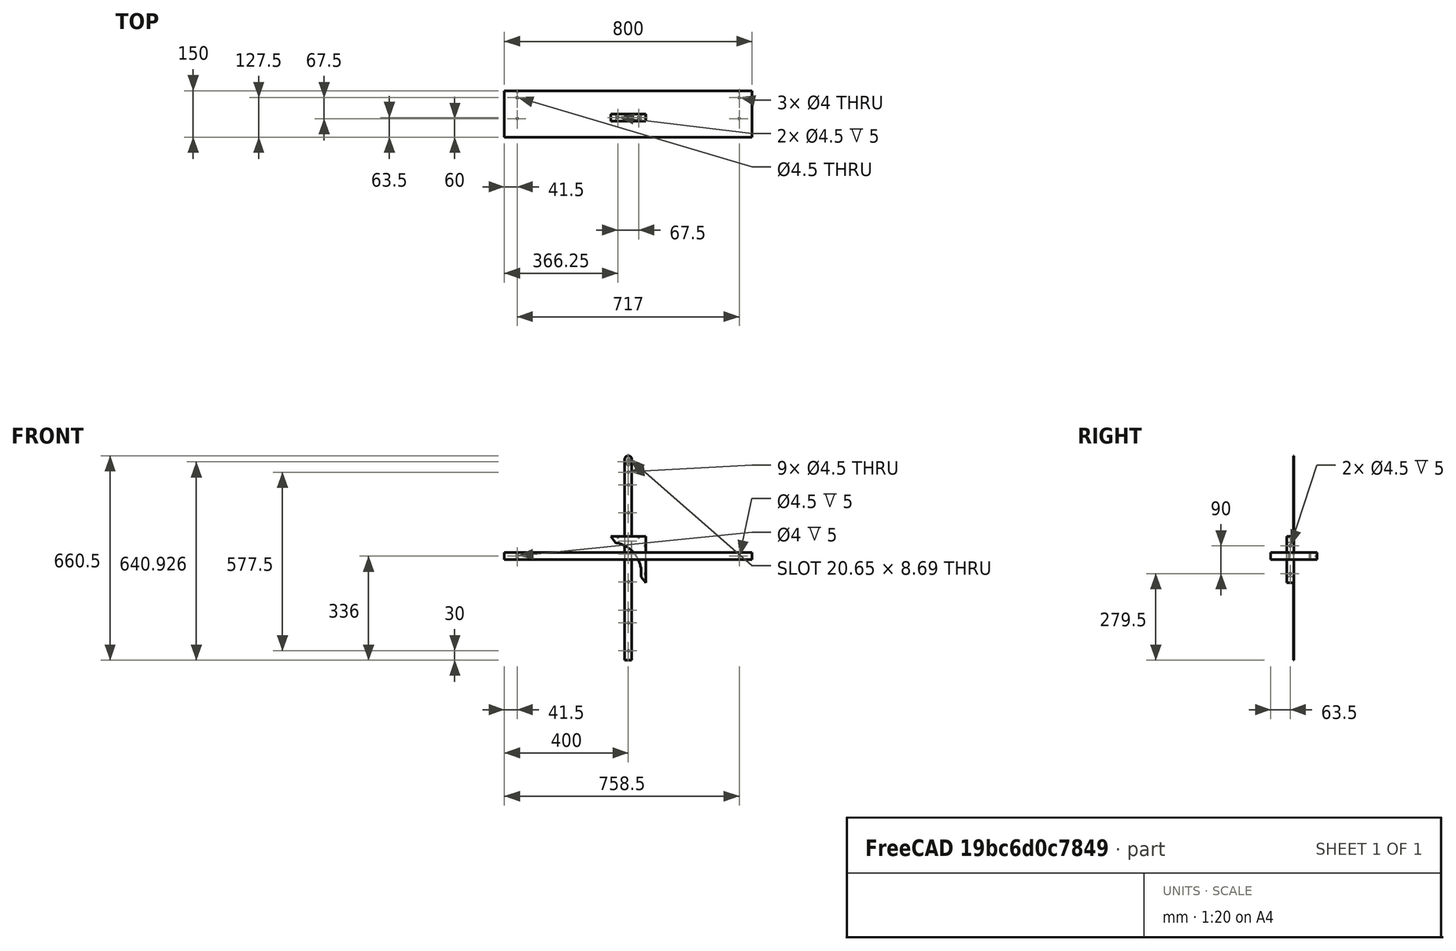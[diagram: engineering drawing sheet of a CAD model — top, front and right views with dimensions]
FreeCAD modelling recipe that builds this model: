
FCSTD DOCUMENT  (FreeCAD 1.0R39109 (Git))
Label: shelf
License: All rights reserved
LicenseURL: https://en.wikipedia.org/wiki/All_rights_reserved
objects: App::FeaturePython×30, TechDraw::DrawViewDimension×30, App::Link×11, Sketcher::SketchObject×7, PartDesign::Pocket×4, TechDraw::DrawProjGroupItem×4, PartDesign::Pad×3, PartDesign::Body×3, TechDraw::DrawSVGTemplate×3, TechDraw::DrawPage×3, Spreadsheet::Sheet×1, TechDraw::DrawProjGroup×1, Assembly::JointGroup×1, Assembly::AssemblyObject×1
note: 84 computed .brp shape members not serialized (recipe doc carries the construction recipe); baked Part::Feature solids carry a one-line shape summary decoded from their .brp

FEATURE [Sketcher::SketchObject] Sketch  label="Top view"
  ArcFitTolerance = 1e-06
  AttachmentSupport = -> [XY_Plane]
  FullyConstrained = true
  MakeInternals = false
  MapMode = 5
  expr: Constraints[12] = <<data>>.pw
  expr: Constraints[13] = <<data>>.pl
  sketch-geometry (6):
    g0: LineSegment StartX=400 StartY=-75 StartZ=0 EndX=400 EndY=75 EndZ=0
    g1: LineSegment StartX=400 StartY=75 StartZ=0 EndX=-400 EndY=75 EndZ=0
    g2: LineSegment StartX=-400 StartY=75 StartZ=0 EndX=-400 EndY=-75 EndZ=0
    g3: LineSegment StartX=-400 StartY=-75 StartZ=0 EndX=400 EndY=-75 EndZ=0
    g4: GeomPoint [constr] X=-2.3e-15 Y=75 Z=0
    g5: GeomPoint [constr] X=400 Y=0 Z=0
  constraints (14):
    c: Coincident(g0,g1)
    c: Coincident(g1,g2)
    c: Coincident(g2,g3)
    c: Coincident(g3,g0)
    c: Vertical(g0)
    c: Vertical(g2)
    c: Horizontal(g1)
    c: Horizontal(g3)
    c: Symmetric(g1,g1,g4)
    c: Symmetric(g0,g0,g5)
    c: Vertical(g4,g-1)
    c: Horizontal(g5,g-1)
    c: DistanceY(g2,g2) = 150
    c: DistanceX(g3,g3) = 800
FEATURE [Spreadsheet::Sheet] Spreadsheet  label="data"
  cells = A1='plank thickness; B1(pt)==23 mm; D1='strip top length; E1(stl)==3 cm; A2='plank length; B2(pl)==80 cm; D2='screw diameter; E2(sd)==4.5 mm; A3='plank width; B3(pw)==15 cm; A4='plank spacing; B4(ps)==20 cm; A5='strip thickness; B5(strip_thickness)==2 mm; A7='triangle ratio; B7(tr)==3 / 4; A8='hole ratio; B8(hr)==1 / 5; A9='triangle hole distance; B9(thd)==(1 - hr * 2) * ps * tr; D9='triangle plank hole distance; E9(tphd)==(1 - hr * 2) * pw * tr; A10='triangle holes pair interval; B10(thpi)==2 * ps * tr * hr + ps * (1 - tr) + pt; A12='tirangle shift; B12(ts)==30 mm
FEATURE [PartDesign::Pad] Pad
  Direction = (0,0,1)
  Length = 23
  Length2 = 10
  Profile = -> Sketch
  ReferenceAxis = -> Sketch [N_Axis]
  Refine = true
  Suppressed = false
  Type = 0
  expr: Length = <<data>>.pt
FEATURE [Sketcher::SketchObject] Sketch001  label="Top view001"
  ArcFitTolerance = 1e-06
  AttachmentSupport = -> [XZ_Plane001]
  FullyConstrained = true
  MakeInternals = false
  MapMode = 5
  Placement = pos=(0,0,0) rot=(1,0,0;1.5708rad)
  expr: Constraints[14] = <<data>>.pw * <<data>>.tr
  expr: Constraints[15] = <<data>>.ps * <<data>>.tr
  sketch-geometry (10):
    g0: LineSegment [constr] StartX=-56.25 StartY=75 StartZ=0 EndX=-56.25 EndY=-75 EndZ=0
    g1: LineSegment [constr] StartX=-56.25 StartY=-75 StartZ=0 EndX=56.25 EndY=-75 EndZ=0
    g2: LineSegment StartX=56.25 StartY=-75 StartZ=0 EndX=56.25 EndY=75 EndZ=0
    g3: LineSegment StartX=56.25 StartY=75 StartZ=0 EndX=-56.25 EndY=75 EndZ=0
    g4: LineSegment [constr] StartX=-56.25 StartY=75 StartZ=0 EndX=56.25 EndY=-75 EndZ=0
    g5: GeomPoint [constr] X=0 Y=75 Z=0
    g6: GeomPoint [constr] X=56.25 Y=0 Z=0
    g7: ArcOfCircle CenterX=-56.25 CenterY=-42.1875 CenterZ=0 NormalX=0 NormalY=0 NormalZ=1 AngleXU=0 Radius=98.3382 StartAngle=6.15252 EndAngle=7.70085
    g8: LineSegment StartX=-56.25 StartY=75 StartZ=0 EndX=-41.25 EndY=55 EndZ=0
    g9: LineSegment StartX=41.25 StartY=-55 StartZ=0 EndX=56.25 EndY=-75 EndZ=0
  constraints (25):
    c: Coincident(g0,g1)
    c: Coincident(g1,g2)
    c: Coincident(g2,g3)
    c: Coincident(g3,g0)
    c: Vertical(g0)
    c: Vertical(g2)
    c: Horizontal(g1)
    c: Horizontal(g3)
    c: Coincident(g4,g0)
    c: Coincident(g4,g1)
    c: Symmetric(g3,g3,g5)
    c: Symmetric(g2,g2,g6)
    c: Vertical(g5,g-1)
    c: Horizontal(g6,g-1)
    c: DistanceX(g3,g3) = 112.5
    c: DistanceY(g2,g2) = 150
    c: PointOnObject(g7,g4)
    c: PointOnObject(g7,g4)
    c: Coincident(g8,g0)
    c: Coincident(g8,g7)
    c: Coincident(g9,g7)
    c: Coincident(g9,g1)
    c: Distance(g9,g9) = 25
    c: Equal(g8,g9)
    c: PointOnObject(g7,g0)
FEATURE [PartDesign::Pad] Pad001
  Direction = (0,-1,2e-16)
  Length = 23
  Length2 = 10
  Placement = pos=(0,0,0) rot=(1,0,0;1.5708rad)
  Profile = -> Sketch001
  ReferenceAxis = -> Sketch001 [N_Axis]
  Refine = true
  Suppressed = false
  Type = 0
  expr: Length = <<data>>.pt
FEATURE [Sketcher::SketchObject] Sketch002
  ArcFitTolerance = 1e-06
  AttachmentSupport = -> [XZ_Plane002]
  FullyConstrained = true
  MakeInternals = false
  MapMode = 5
  Placement = pos=(0,0,0) rot=(1,0,0;1.5708rad)
  expr: Constraints[10] = <<data>>.pt
  expr: Constraints[11] = <<data>>.stl + <<data>>.pt * 3 + <<data>>.ps * 2 + <<data>>.tr * <<data>>.ps
  expr: Constraints[17] = <<data>>.sd
  expr: Constraints[18] = <<data>>.stl + <<data>>.pt + <<data>>.ps * <<data>>.tr / 5
  expr: Constraints[20] = <<data>>.sd
  expr: Constraints[21] = <<data>>.thd
  expr: Constraints[23] = <<data>>.thpi
  expr: Constraints[24] = <<data>>.sd
  expr: Constraints[26] = <<data>>.sd
  expr: Constraints[27] = <<data>>.thd
  expr: Constraints[29] = <<data>>.sd
  expr: Constraints[31] = <<data>>.sd
  expr: Constraints[32] = <<data>>.thd
  expr: Constraints[33] = <<data>>.thpi
  expr: Constraints[36] = <<data>>.pt / 2 + <<data>>.ps * <<data>>.tr * <<data>>.hr
  expr: Constraints[38] = <<data>>.sd
  expr: Constraints[39] = <<data>>.pt / 2 + <<data>>.ps * <<data>>.tr * <<data>>.hr
  expr: Constraints[41] = <<data>>.sd
  expr: Constraints[42] = <<data>>.pt / 2 + <<data>>.ps * <<data>>.tr * <<data>>.hr
  expr: Constraints[46] = <<data>>.sd
  expr: Constraints[52] = <<data>>.sd
  expr: Constraints[53] = 10 mm
  sketch-geometry (20):
    g0: LineSegment StartX=-11.5 StartY=324.5 StartZ=0 EndX=-11.5 EndY=-324.5 EndZ=0
    g1: LineSegment StartX=-11.5 StartY=-324.5 StartZ=0 EndX=11.5 EndY=-324.5 EndZ=0
    g2: LineSegment StartX=11.5 StartY=-324.5 StartZ=0 EndX=11.5 EndY=324.5 EndZ=0
    g3: LineSegment [constr] StartX=11.5 StartY=324.5 StartZ=0 EndX=-11.5 EndY=324.5 EndZ=0
    g4: ArcOfCircle CenterX=-4e-16 CenterY=324.5 CenterZ=0 NormalX=0 NormalY=0 NormalZ=1 AngleXU=0 Radius=11.5 StartAngle=0 EndAngle=3.14159
    g5: GeomPoint X=-11.5 Y=0 Z=0
    g6: GeomPoint X=0 Y=-324.5 Z=0
    g7: Circle CenterX=0 CenterY=241.5 CenterZ=0 NormalX=0 NormalY=0 NormalZ=1 AngleXU=0 Radius=2.25
    g8: Circle CenterX=0 CenterY=151.5 CenterZ=0 NormalX=0 NormalY=0 NormalZ=1 AngleXU=0 Radius=2.25
    g9: Circle CenterX=0 CenterY=18.5 CenterZ=0 NormalX=0 NormalY=0 NormalZ=1 AngleXU=0 Radius=2.25
    g10: Circle CenterX=0 CenterY=-71.5 CenterZ=0 NormalX=0 NormalY=0 NormalZ=1 AngleXU=0 Radius=2.25
    g11: Circle CenterX=0 CenterY=-204.5 CenterZ=0 NormalX=0 NormalY=0 NormalZ=1 AngleXU=0 Radius=2.25
    g12: Circle CenterX=0 CenterY=-294.5 CenterZ=0 NormalX=0 NormalY=0 NormalZ=1 AngleXU=0 Radius=2.25
    g13: Circle CenterX=0 CenterY=283 CenterZ=0 NormalX=0 NormalY=0 NormalZ=1 AngleXU=0 Radius=2.25
    g14: Circle CenterX=0 CenterY=60 CenterZ=0 NormalX=0 NormalY=0 NormalZ=1 AngleXU=0 Radius=2.25
    g15: Circle CenterX=0 CenterY=-163 CenterZ=0 NormalX=0 NormalY=0 NormalZ=1 AngleXU=0 Radius=2.25
    g16: ArcOfCircle CenterX=-4e-16 CenterY=324.5 CenterZ=0 NormalX=0 NormalY=0 NormalZ=1 AngleXU=0 Radius=2.25 StartAngle=-1.15e-14 EndAngle=3.14159
    g17: LineSegment StartX=2.25 StartY=324.5 StartZ=0 EndX=2.25 EndY=314.5 EndZ=0
    g18: LineSegment StartX=-2.25 StartY=324.5 StartZ=0 EndX=-2.25 EndY=314.5 EndZ=0
    g19: ArcOfCircle CenterX=0 CenterY=310.603 CenterZ=0 NormalX=0 NormalY=0 NormalZ=1 AngleXU=0 Radius=4.5 StartAngle=2.0944 EndAngle=7.33038
  constraints (54):
    c: Coincident(g0,g1)
    c: Coincident(g1,g2)
    c: Coincident(g2,g3)
    c: Coincident(g3,g0)
    c: Vertical(g0)
    c: Vertical(g2)
    c: Horizontal(g1)
    c: Horizontal(g3)
    c: Coincident(g4,g2)
    c: Tangent(g4,g0) = -1.5708
    c: DistanceX(g1,g1) = 23
    c: DistanceY(g2,g2) = 649
    c: Symmetric(g0,g0,g5)
    c: Symmetric(g1,g1,g6)
    c: Horizontal(g5,g-1)
    c: Vertical(g6,g-1)
    c: PointOnObject(g7,g-2)
    c: Diameter(g7) = 4.5
    c: DistanceY(g7,g4) = 83
    c: PointOnObject(g8,g-2)
    c: Diameter(g8) = 4.5
    c: DistanceY(g8,g7) = 90
    c: PointOnObject(g9,g-2)
    c: DistanceY(g9,g8) = 133
    c: Diameter(g9) = 4.5
    c: PointOnObject(g10,g-2)
    c: Diameter(g10) = 4.5
    c: DistanceY(g10,g9) = 90
    c: PointOnObject(g11,g-2)
    c: Diameter(g11) = 4.5
    c: PointOnObject(g12,g-2)
    c: Diameter(g12) = 4.5
    c: DistanceY(g12,g11) = 90
    c: DistanceY(g11,g10) = 133
    c: PointOnObject(g13,g-2)
    c: Equal(g13,g7)
    c: DistanceY(g7,g13) = 41.5
    c: PointOnObject(g14,g-2)
    c: Diameter(g14) = 4.5
    c: DistanceY(g9,g14) = 41.5
    c: PointOnObject(g15,g-2)
    c: Diameter(g15) = 4.5
    c: DistanceY(g11,g15) = 41.5
    c: Tangent(g16,g17) = 1.5708
    c: Tangent(g16,g18) = -1.5708
    c: Vertical(g18)
    c: Distance(g16,g16) = 4.5
    c: Coincident(g16,g4)
    c: Vertical(g17)
    c: PointOnObject(g19,g-2)
    c: Coincident(g19,g17)
    c: Coincident(g19,g18)
    c: Radius(g19) = 4.5
    c: DistanceY(g17,g16) = 10
FEATURE [PartDesign::Pad] Pad002
  Direction = (0,-1,2e-16)
  Length = 2
  Length2 = 10
  Placement = pos=(0,0,0) rot=(1,0,0;1.5708rad)
  Profile = -> Sketch002
  ReferenceAxis = -> Sketch002 [N_Axis]
  Refine = true
  Suppressed = false
  Type = 0
  expr: Length = <<data>>.strip_thickness
FEATURE [PartDesign::Body] Body002  label="Strip"
  AllowCompound = false
  Group = -> [Sketch002,Pad002]
  Origin = -> Origin002
  Tip = -> Pad002
FEATURE [Sketcher::SketchObject] Sketch003
  ArcFitTolerance = 1e-06
  AttachmentSupport = -> [Pad001]
  ExternalGeometry = -> [Pad001]
  FullyConstrained = true
  MakeInternals = false
  MapMode = 5
  Placement = pos=(56.25,0,0) rot=(0.707107,0,0.707107;3.14159rad)
  expr: Constraints[5] = <<data>>.sd
  expr: Constraints[6] = <<data>>.hr * <<data>>.ps * <<data>>.tr
  expr: Constraints[8] = <<data>>.sd
  expr: Constraints[9] = <<data>>.thd
  sketch-geometry (5):
    g0: GeomPoint X=-75 Y=11.5 Z=0
    g1: GeomPoint X=75 Y=11.5 Z=0
    g2: LineSegment [constr] StartX=-75 StartY=11.5 StartZ=0 EndX=75 EndY=11.5 EndZ=0
    g3: Circle CenterX=-45 CenterY=11.5 CenterZ=0 NormalX=0 NormalY=0 NormalZ=1 AngleXU=0 Radius=2.25
    g4: Circle CenterX=45 CenterY=11.5 CenterZ=0 NormalX=0 NormalY=0 NormalZ=1 AngleXU=0 Radius=2.25
  constraints (10):
    c: Symmetric(g-4,g-4,g0)
    c: Symmetric(g-6,g-6,g1)
    c: Coincident(g2,g0)
    c: Coincident(g2,g1)
    c: PointOnObject(g3,g2)
    c: Diameter(g3) = 4.5
    c: Distance(g3,g0) = 30
    c: PointOnObject(g4,g2)
    c: Diameter(g4) = 4.5
    c: DistanceX(g3,g4) = 90
FEATURE [PartDesign::Pocket] Pocket
  BaseFeature = -> Pad001
  Direction = (-1,0,2e-16)
  Length = 5
  Length2 = 5
  Placement = pos=(0,0,0) rot=(1,0,0;1.5708rad)
  Profile = -> Sketch003
  ReferenceAxis = -> Sketch003 [N_Axis]
  Refine = true
  Suppressed = false
  Type = 0
FEATURE [Sketcher::SketchObject] Sketch004
  ArcFitTolerance = 1e-06
  AttachmentSupport = -> [Pocket]
  ExternalGeometry = -> [Pocket]
  FullyConstrained = true
  MakeInternals = false
  MapMode = 5
  Placement = pos=(0,1.67e-14,75) rot=(0,0,1;3.14159rad)
  expr: Constraints[6] = <<data>>.sd
  expr: Constraints[7] = <<data>>.sd
  expr: Constraints[8] = <<data>>.pw * <<data>>.tr * <<data>>.hr
  expr: Constraints[9] = <<data>>.tphd
  sketch-geometry (5):
    g0: GeomPoint X=-56.25 Y=11.5 Z=0
    g1: GeomPoint X=56.25 Y=11.5 Z=0
    g2: LineSegment [constr] StartX=-56.25 StartY=11.5 StartZ=0 EndX=56.25 EndY=11.5 EndZ=0
    g3: Circle CenterX=-33.75 CenterY=11.5 CenterZ=0 NormalX=0 NormalY=0 NormalZ=1 AngleXU=0 Radius=2.25
    g4: Circle CenterX=33.75 CenterY=11.5 CenterZ=0 NormalX=0 NormalY=0 NormalZ=1 AngleXU=0 Radius=2.25
  constraints (10):
    c: Symmetric(g-4,g-4,g0)
    c: Symmetric(g-6,g-6,g1)
    c: Coincident(g2,g0)
    c: Symmetric(g-6,g-6,g2)
    c: PointOnObject(g3,g2)
    c: PointOnObject(g4,g2)
    c: Diameter(g4) = 4.5
    c: Diameter(g3) = 4.5
    c: DistanceX(g0,g3) = 22.5
    c: DistanceX(g3,g4) = 67.5
FEATURE [PartDesign::Pocket] Pocket001
  BaseFeature = -> Pocket
  Direction = (0,0,-1)
  Length = 5
  Length2 = 5
  Placement = pos=(0,0,0) rot=(1,0,0;1.5708rad)
  Profile = -> Sketch004
  ReferenceAxis = -> Sketch004 [N_Axis]
  Refine = true
  Suppressed = false
  Type = 0
FEATURE [PartDesign::Body] Body001  label="Triangle"
  AllowCompound = false
  Group = -> [Sketch001,Pad001,Sketch003,Pocket,Sketch004,Pocket001]
  Origin = -> Origin001
  Tip = -> Pocket001
FEATURE [Sketcher::SketchObject] Sketch005
  ArcFitTolerance = 1e-06
  AttachmentSupport = -> [Pad]
  ExternalGeometry = -> [Pad]
  FullyConstrained = true
  MakeInternals = false
  MapMode = 5
  Placement = pos=(0,0,23) rot=(0,0,1;0rad)
  expr: Constraints[22] = <<data>>.pw * <<data>>.tr * <<data>>.hr
  expr: Constraints[24] = <<data>>.pw - <<data>>.pw * <<data>>.tr * (1 - <<data>>.hr)
  expr: Constraints[25] = <<data>>.pt / 2 + <<data>>.ts
  expr: Constraints[6] = <<data>>.sd
  sketch-geometry (11):
    g0: GeomPoint [constr] X=-358.5 Y=75 Z=0
    g1: GeomPoint [constr] X=-358.5 Y=-75 Z=0
    g2: LineSegment [constr] StartX=-358.5 StartY=75 StartZ=0 EndX=-358.5 EndY=-75 EndZ=0
    g3: Circle CenterX=-358.5 CenterY=52.5 CenterZ=0 NormalX=0 NormalY=0 NormalZ=1 AngleXU=0 Radius=2.25
    g4: LineSegment [constr] StartX=-400 StartY=75 StartZ=0 EndX=-400 EndY=52.5 EndZ=0
    g5: LineSegment [constr] StartX=-400 StartY=52.5 StartZ=0 EndX=-358.5 EndY=52.5 EndZ=0
    g6: LineSegment [constr] StartX=-358.5 StartY=52.5 StartZ=0 EndX=-358.5 EndY=75 EndZ=0
    g7: LineSegment [constr] StartX=-358.5 StartY=75 StartZ=0 EndX=-400 EndY=75 EndZ=0
    g8: Circle CenterX=-358.5 CenterY=-15 CenterZ=0 NormalX=0 NormalY=0 NormalZ=1 AngleXU=0 Radius=2
    g9: Circle CenterX=358.5 CenterY=-15 CenterZ=0 NormalX=0 NormalY=0 NormalZ=1 AngleXU=0 Radius=2
    g10: Circle CenterX=358.5 CenterY=52.5 CenterZ=0 NormalX=0 NormalY=0 NormalZ=1 AngleXU=0 Radius=2
  constraints (26):
    c: PointOnObject(g0,g-3)
    c: PointOnObject(g1,g-5)
    c: Coincident(g2,g0)
    c: Coincident(g2,g1)
    c: Vertical(g2)
    c: PointOnObject(g3,g2)
    c: Diameter(g3) = 4.5
    c: Coincident(g4,g5)
    c: Coincident(g5,g6)
    c: Coincident(g6,g7)
    c: Coincident(g7,g4)
    c: Vertical(g4)
    c: Vertical(g6)
    c: Horizontal(g5)
    c: Horizontal(g7)
    c: Coincident(g4,g-4)
    c: Coincident(g5,g3)
    c: Diameter(g8) = 4
    c: Diameter(g9) = 4
    c: Symmetric(g9,g8,g-2)
    c: Diameter(g10) = 4
    c: Symmetric(g10,g3,g-2)
    c: DistanceY(g3,g0) = 22.5
    c: PointOnObject(g8,g2)
    c: DistanceY(g-5,g8) = 60
    c: Distance(g5,g5) = 41.5
FEATURE [PartDesign::Pocket] Pocket002
  BaseFeature = -> Pad
  Direction = (0,0,-1)
  Length = 23
  Length2 = 5
  Profile = -> Sketch005
  ReferenceAxis = -> Sketch005 [N_Axis]
  Refine = true
  Suppressed = false
  Type = 0
  expr: Length = <<data>>.pt
FEATURE [Sketcher::SketchObject] Sketch006
  ArcFitTolerance = 1e-06
  AttachmentSupport = -> [Pocket002]
  ExternalGeometry = -> [Pocket002]
  FullyConstrained = true
  MakeInternals = false
  MapMode = 5
  Placement = pos=(0,75,0) rot=(0,0.707107,0.707107;3.14159rad)
  expr: Constraints[11] = <<data>>.sd
  expr: Constraints[14] = <<data>>.pt / 2
  expr: Constraints[9] = <<data>>.pt / 2 + <<data>>.ts
  sketch-geometry (6):
    g0: LineSegment [constr] StartX=-400 StartY=23 StartZ=0 EndX=-400 EndY=11.5 EndZ=0
    g1: LineSegment [constr] StartX=-400 StartY=11.5 StartZ=0 EndX=-358.5 EndY=11.5 EndZ=0
    g2: LineSegment [constr] StartX=-358.5 StartY=11.5 StartZ=0 EndX=-358.5 EndY=23 EndZ=0
    g3: LineSegment [constr] StartX=-358.5 StartY=23 StartZ=0 EndX=-400 EndY=23 EndZ=0
    g4: Circle CenterX=-358.5 CenterY=11.5 CenterZ=0 NormalX=0 NormalY=0 NormalZ=1 AngleXU=0 Radius=2.25
    g5: Circle CenterX=358.5 CenterY=11.5 CenterZ=0 NormalX=0 NormalY=0 NormalZ=1 AngleXU=0 Radius=2
  constraints (15):
    c: Coincident(g0,g1)
    c: Coincident(g1,g2)
    c: Coincident(g2,g3)
    c: Coincident(g3,g0)
    c: Vertical(g0)
    c: Vertical(g2)
    c: Horizontal(g1)
    c: Horizontal(g3)
    c: Coincident(g0,g-4)
    c: DistanceX(g3,g3) = 41.5
    c: Coincident(g4,g1)
    c: Diameter(g4) = 4.5
    c: Diameter(g5) = 4
    c: Symmetric(g1,g5,g-2)
    c: DistanceY(g0,g0) = 11.5
FEATURE [PartDesign::Pocket] Pocket003
  BaseFeature = -> Pocket002
  Direction = (0,-1,2e-16)
  Length = 5
  Length2 = 5
  Profile = -> Sketch006
  ReferenceAxis = -> Sketch006 [N_Axis]
  Refine = true
  Suppressed = false
  Type = 0
FEATURE [PartDesign::Body] Body  label="Plank"
  AllowCompound = false
  Group = -> [Sketch,Pad,Sketch005,Pocket002,Sketch006,Pocket003]
  Origin = -> Origin
  Tip = -> Pocket003
FEATURE [App::Link] Strip  label="Strip001"
  LinkPlacement = pos=(0,0,0) rot=(-0.169876,-0.511926,-0.842065;0.275078rad)
  LinkedObject = -> Body002
  Placement = pos=(0,0,0) rot=(-0.169876,-0.511926,-0.842065;0.275078rad)
FEATURE [App::Link] Strip001  label="Strip002"
  LinkPlacement = pos=(690.822,-161.651,103.555) rot=(-0.169876,-0.511926,-0.842065;0.275078rad)
  LinkedObject = -> Body002
  Placement = pos=(690.822,-161.651,103.555) rot=(-0.169876,-0.511926,-0.842065;0.275078rad)
FEATURE [App::Link] Triangle  label="Triangle001"
  LinkPlacement = pos=(27.6721,50.4445,-26.2331) rot=(-0.042214,0.084144,0.995559;4.476rad)
  LinkedObject = -> Body001
  Placement = pos=(27.6721,50.4445,-26.2331) rot=(-0.042214,0.084144,0.995559;4.476rad)
FEATURE [App::Link] Triangle001  label="Triangle002"
  LinkPlacement = pos=(-2.13692,64.3482,194.328) rot=(-0.042214,0.084144,0.995559;4.476rad)
  LinkedObject = -> Body001
  Placement = pos=(-2.13692,64.3482,194.328) rot=(-0.042214,0.084144,0.995559;4.476rad)
FEATURE [App::Link] Triangle002  label="Triangle003"
  LinkPlacement = pos=(688.685,-97.3025,297.883) rot=(-0.042214,0.084144,0.995559;4.476rad)
  LinkedObject = -> Body001
  Placement = pos=(688.685,-97.3025,297.883) rot=(-0.042214,0.084144,0.995559;4.476rad)
FEATURE [App::Link] Triangle003  label="Triangle004"
  LinkPlacement = pos=(718.494,-111.206,77.3222) rot=(-0.042214,0.084144,0.995559;4.476rad)
  LinkedObject = -> Body001
  Placement = pos=(718.494,-111.206,77.3222) rot=(-0.042214,0.084144,0.995559;4.476rad)
FEATURE [App::Link] Triangle004  label="Triangle005"
  LinkPlacement = pos=(748.303,-125.11,-143.239) rot=(-0.042214,0.084144,0.995559;4.476rad)
  LinkedObject = -> Body001
  Placement = pos=(748.303,-125.11,-143.239) rot=(-0.042214,0.084144,0.995559;4.476rad)
FEATURE [App::Link] Triangle005  label="Triangle006"
  LinkPlacement = pos=(57.4811,36.5407,-246.794) rot=(-0.042214,0.084144,0.995559;4.476rad)
  LinkedObject = -> Body001
  Placement = pos=(57.4811,36.5407,-246.794) rot=(-0.042214,0.084144,0.995559;4.476rad)
FEATURE [App::Link] Plank  label="Plank001"
  LinkPlacement = pos=(356.327,-4.88218,97.502) rot=(-0.070661,0.023448,0.997225;2.91017rad)
  LinkedObject = -> Body
  Placement = pos=(356.327,-4.88218,97.502) rot=(-0.070661,0.023448,0.997225;2.91017rad)
FEATURE [App::Link] Plank001  label="Plank002"
  LinkPlacement = pos=(386.136,-18.7859,-123.059) rot=(-0.070661,0.023448,0.997225;2.91017rad)
  LinkedObject = -> Body
  Placement = pos=(386.136,-18.7859,-123.059) rot=(-0.070661,0.023448,0.997225;2.91017rad)
FEATURE [App::Link] Plank002  label="Plank003"
  LinkPlacement = pos=(323.444,10.4556,340.811) rot=(0.990825,-0.115483,0.070207;3.09501rad)
  LinkedObject = -> Body
  Placement = pos=(323.444,10.4556,340.811) rot=(0.990825,-0.115483,0.070207;3.09501rad)
FEATURE [App::FeaturePython] GroundedJoint  # Assembly grounded joint (typed FeaturePython)
  ObjectToGround = -> Strip
  Placement = pos=(0,0,0) rot=(-0.169876,-0.511926,-0.842065;0.275078rad)
FEATURE [App::FeaturePython] Joint  label="Parallel"  # Assembly joint (typed FeaturePython)
  Activated = true
  AngleMax = 0
  AngleMin = 0
  Detach1 = false
  Detach2 = false
  Distance = 0
  Distance2 = 0
  EnableAngleMax = false
  EnableAngleMin = false
  EnableLengthMax = false
  EnableLengthMin = false
  JointType = 6 (Parallel)
  LengthMax = 0
  LengthMin = 0
  Placement1 = pos=(56.25,-11.5,0) rot=(0,-1,0;1.5708rad)
  Placement2 = pos=(-6e-15,-2,151.5) rot=(0.57735,0.57735,0.57735;4.18879rad)
  Reference1 = -> Assembly [Triangle001.Face3,Triangle001.Face3]
  Reference2 = -> Assembly [Strip.Face19,Strip.Edge11]
FEATURE [App::FeaturePython] Joint001  label="Perpendicular"  # Assembly joint (typed FeaturePython)
  Activated = true
  AngleMax = 0
  AngleMin = 0
  Detach1 = false
  Detach2 = false
  Distance = 0
  Distance2 = 0
  EnableAngleMax = false
  EnableAngleMin = false
  EnableLengthMax = false
  EnableLengthMin = false
  JointType = 7 (Perpendicular)
  LengthMax = 0
  LengthMin = 0
  Placement1 = pos=(-7.1e-15,-11.5,75) rot=(0,-1,0;3.14159rad)
  Placement2 = pos=(-1.9e-15,3.55e-14,151.5) rot=(0.57735,0.57735,0.57735;4.18879rad)
  Reference1 = -> Assembly [Triangle001.Face7,Triangle001.Face7]
  Reference2 = -> Assembly [Strip.Face18,Strip.Edge11]
FEATURE [App::FeaturePython] Joint002  label="Parallel001"  # Assembly joint (typed FeaturePython)
  Activated = true
  AngleMax = 0
  AngleMin = 0
  Detach1 = false
  Detach2 = false
  Distance = 0
  Distance2 = 0
  EnableAngleMax = false
  EnableAngleMin = false
  EnableLengthMax = false
  EnableLengthMin = false
  JointType = 6 (Parallel)
  LengthMax = 0
  LengthMin = 0
  Placement1 = pos=(23.1803,1.07e-14,33.3377) rot=(-0.57735,-0.57735,-0.57735;2.0944rad)
  Placement2 = pos=(11.5,-1,2.9e-15) rot=(0,-1,0;1.5708rad)
  Reference1 = -> Assembly [Triangle001.Face4,Triangle001.Face4]
  Reference2 = -> Assembly [Strip.Face3,Strip.Face3]
FEATURE [App::FeaturePython] Joint003  label="Fixed"  # Assembly joint (typed FeaturePython)
  Activated = true
  AngleMax = 0
  AngleMin = 0
  Detach1 = false
  Detach2 = false
  Distance = 0
  Distance2 = 0
  EnableAngleMax = false
  EnableAngleMin = false
  EnableLengthMax = false
  EnableLengthMin = false
  JointType = 0 (Fixed)
  LengthMax = 0
  LengthMin = 0
  Placement1 = pos=(-3.7e-15,5.59e-14,241.5) rot=(1,0,0;1.5708rad)
  Placement2 = pos=(56.25,-11.5,45) rot=(-0.707107,0,-0.707107;3.14159rad)
  Reference1 = -> Assembly [Strip.Edge35,Strip.Edge35]
  Reference2 = -> Assembly [Triangle001.Edge12,Triangle001.Edge12]
FEATURE [App::FeaturePython] Joint004  label="Parallel002"  # Assembly joint (typed FeaturePython)
  Activated = true
  AngleMax = 0
  AngleMin = 0
  Detach1 = false
  Detach2 = false
  Distance = 0
  Distance2 = 0
  EnableAngleMax = false
  EnableAngleMin = false
  EnableLengthMax = false
  EnableLengthMin = false
  JointType = 6 (Parallel)
  LengthMax = 0
  LengthMin = 0
  Placement1 = pos=(3e-16,-2,2.14715) rot=(0.57735,0.57735,0.57735;4.18879rad)
  Placement2 = pos=(1.137e-13,-2,2.14715) rot=(0.57735,0.57735,0.57735;4.18879rad)
  Reference1 = -> Assembly [Strip.Face19,Strip.Face19]
  Reference2 = -> Assembly [Strip001.Face19,Strip001.Face19]
FEATURE [App::FeaturePython] Joint005  label="Parallel003"  # Assembly joint (typed FeaturePython)
  Activated = true
  AngleMax = 0
  AngleMin = 0
  Detach1 = false
  Detach2 = false
  Distance = 0
  Distance2 = 0
  EnableAngleMax = false
  EnableAngleMin = false
  EnableLengthMax = false
  EnableLengthMin = false
  JointType = 6 (Parallel)
  LengthMax = 0
  LengthMin = 0
  Placement1 = pos=(-11.5,-1,7.4e-15) rot=(0,1,0;1.5708rad)
  Placement2 = pos=(11.5,-1,2.9e-15) rot=(0,-1,0;1.5708rad)
  Reference1 = -> Assembly [Strip001.Face1,Strip001.Face1]
  Reference2 = -> Assembly [Strip.Face3,Strip.Face3]
FEATURE [App::FeaturePython] Joint006  label="Parallel004"  # Assembly joint (typed FeaturePython)
  Activated = true
  AngleMax = 0
  AngleMin = 0
  Detach1 = false
  Detach2 = false
  Distance = 0
  Distance2 = 0
  EnableAngleMax = false
  EnableAngleMin = false
  EnableLengthMax = false
  EnableLengthMin = false
  JointType = 6 (Parallel)
  LengthMax = 0
  LengthMin = 0
  Placement1 = pos=(0,-1,-324.5) rot=(0,0,1;0rad)
  Placement2 = pos=(2e-15,-1,-324.5) rot=(0,0,1;0rad)
  Reference1 = -> Assembly [Strip001.Face2,Strip001.Face2]
  Reference2 = -> Assembly [Strip.Face2,Strip.Face2]
FEATURE [App::FeaturePython] Joint008  label="Perpendicular001"  # Assembly joint (typed FeaturePython)
  Activated = true
  AngleMax = 0
  AngleMin = 0
  Detach1 = false
  Detach2 = false
  Distance = 0
  Distance2 = 0
  EnableAngleMax = false
  EnableAngleMin = false
  EnableLengthMax = false
  EnableLengthMin = false
  JointType = 7 (Perpendicular)
  LengthMax = 0
  LengthMin = 0
  Placement1 = pos=(23.1803,-23,33.3377) rot=(-0.57735,-0.57735,-0.57735;2.0944rad)
  Placement2 = pos=(-4.4e-15,2.5e-15,2.14715) rot=(0.57735,0.57735,0.57735;4.18879rad)
  Reference1 = -> Assembly [Triangle.Face5,Triangle.Face5]
  Reference2 = -> Assembly [Strip.Face18,Strip.Face18]
FEATURE [App::FeaturePython] Joint009  label="Parallel005"  # Assembly joint (typed FeaturePython)
  Activated = true
  AngleMax = 0
  AngleMin = 0
  Detach1 = false
  Detach2 = false
  Distance = 0
  Distance2 = 0
  EnableAngleMax = false
  EnableAngleMin = false
  EnableLengthMax = false
  EnableLengthMin = false
  JointType = 6 (Parallel)
  LengthMax = 0
  LengthMin = 0
  Placement1 = pos=(56.25,-11.5,3.6e-15) rot=(0,-1,0;1.5708rad)
  Placement2 = pos=(-4.4e-15,2.5e-15,2.14715) rot=(0.57735,0.57735,0.57735;4.18879rad)
  Reference1 = -> Assembly [Triangle.Face3,Triangle.Face3]
  Reference2 = -> Assembly [Strip.Face18,Strip.Face18]
FEATURE [App::FeaturePython] Joint010  label="Fixed001"  # Assembly joint (typed FeaturePython)
  Activated = true
  AngleMax = 0
  AngleMin = 0
  Detach1 = false
  Detach2 = false
  Distance = 0
  Distance2 = 0
  EnableAngleMax = false
  EnableAngleMin = false
  EnableLengthMax = false
  EnableLengthMin = false
  JointType = 0 (Fixed)
  LengthMax = 0
  LengthMin = 0
  Placement1 = pos=(56.25,-11.5,45) rot=(-0.707107,0,-0.707107;3.14159rad)
  Placement2 = pos=(3e-16,4.2e-15,18.5) rot=(1,0,0;1.5708rad)
  Reference1 = -> Assembly [Triangle.Edge12,Triangle.Edge12]
  Reference2 = -> Assembly [Strip.Edge41,Strip.Edge41]
FEATURE [App::FeaturePython] Joint011  label="Parallel006"  # Assembly joint (typed FeaturePython)
  Activated = true
  AngleMax = 0
  AngleMin = 0
  Detach1 = false
  Detach2 = false
  Distance = 0
  Distance2 = 0
  EnableAngleMax = false
  EnableAngleMin = false
  EnableLengthMax = false
  EnableLengthMin = false
  JointType = 6 (Parallel)
  LengthMax = 0
  LengthMin = 0
  Placement1 = pos=(56.25,-11.5,-75) rot=(-0.57735,-0.57735,0.57735;4.18879rad)
  Placement2 = pos=(2e-16,-7.53e-14,-324.5) rot=(0.707107,0,0.707107;3.14159rad)
  Reference1 = -> Assembly [Triangle.Edge2,Triangle.Edge2]
  Reference2 = -> Assembly [Strip.Edge6,Strip.Edge6]
FEATURE [App::FeaturePython] Joint012  label="Parallel007"  # Assembly joint (typed FeaturePython)
  Activated = true
  AngleMax = 0
  AngleMin = 0
  Detach1 = false
  Detach2 = false
  Distance = 0
  Distance2 = 0
  EnableAngleMax = false
  EnableAngleMin = false
  EnableLengthMax = false
  EnableLengthMin = false
  JointType = 6 (Parallel)
  LengthMax = 0
  LengthMin = 0
  Placement1 = pos=(0,-1.3e-14,2.14715) rot=(0.57735,0.57735,0.57735;4.18879rad)
  Placement2 = pos=(56.25,-11.5,0) rot=(0,-1,0;1.5708rad)
  Reference1 = -> Assembly [Strip001.Face18,Strip001.Face18]
  Reference2 = -> Assembly [Triangle002.Face3,Triangle002.Face3]
FEATURE [App::FeaturePython] Joint013  label="Parallel008"  # Assembly joint (typed FeaturePython)
  Activated = true
  AngleMax = 0
  AngleMin = 0
  Detach1 = false
  Detach2 = false
  Distance = 0
  Distance2 = 0
  EnableAngleMax = false
  EnableAngleMin = false
  EnableLengthMax = false
  EnableLengthMin = false
  JointType = 6 (Parallel)
  LengthMax = 0
  LengthMin = 0
  Placement1 = pos=(56.25,-11.5,-75) rot=(-0.57735,-0.57735,0.57735;4.18879rad)
  Placement2 = pos=(-1.137e-13,-8.66e-14,-324.5) rot=(0.707107,0,0.707107;3.14159rad)
  Reference1 = -> Assembly [Triangle002.Edge2,Triangle002.Edge2]
  Reference2 = -> Assembly [Strip001.Edge6,Strip001.Edge6]
FEATURE [App::FeaturePython] Joint014  label="Fixed002"  # Assembly joint (typed FeaturePython)
  Activated = true
  AngleMax = 0
  AngleMin = 0
  Detach1 = false
  Detach2 = false
  Distance = 0
  Distance2 = 0
  EnableAngleMax = false
  EnableAngleMin = false
  EnableLengthMax = false
  EnableLengthMin = false
  JointType = 0 (Fixed)
  LengthMax = 0
  LengthMin = 0
  Placement1 = pos=(56.25,-11.5,45) rot=(-0.707107,0,-0.707107;3.14159rad)
  Placement2 = pos=(1.137e-13,6.8e-14,241.5) rot=(1,0,0;1.5708rad)
  Reference1 = -> Assembly [Triangle002.Edge12,Triangle002.Edge12]
  Reference2 = -> Assembly [Strip001.Edge35,Strip001.Edge35]
FEATURE [App::FeaturePython] Joint015  label="Parallel009"  # Assembly joint (typed FeaturePython)
  Activated = true
  AngleMax = 0
  AngleMin = 0
  Detach1 = false
  Detach2 = false
  Distance = 0
  Distance2 = 0
  EnableAngleMax = false
  EnableAngleMin = false
  EnableLengthMax = false
  EnableLengthMin = false
  JointType = 6 (Parallel)
  LengthMax = 0
  LengthMin = 0
  Placement1 = pos=(0.00997656,-0.00931849,0) rot=(0,0,1;0rad)
  Placement2 = pos=(1.42e-14,-11.5,75) rot=(0,-1,0;3.14159rad)
  Reference1 = -> Assembly [Plank002.Face4,Plank002.Face4]
  Reference2 = -> Assembly [Triangle002.Face7,Triangle002.Face7]
FEATURE [App::FeaturePython] Joint016  label="Parallel010"  # Assembly joint (typed FeaturePython)
  Activated = true
  AngleMax = 0
  AngleMin = 0
  Detach1 = false
  Detach2 = false
  Distance = 0
  Distance2 = 0
  EnableAngleMax = false
  EnableAngleMin = false
  EnableLengthMax = false
  EnableLengthMin = false
  JointType = 6 (Parallel)
  LengthMax = 0
  LengthMin = 0
  Placement1 = pos=(-0.0651362,75,11.5) rot=(0,0.707107,-0.707107;3.14159rad)
  Placement2 = pos=(0,-1.3e-14,2.14715) rot=(0.57735,0.57735,0.57735;4.18879rad)
  Reference1 = -> Assembly [Plank002.Face3,Plank002.Face3]
  Reference2 = -> Assembly [Strip001.Face18,Strip001.Face18]
FEATURE [App::FeaturePython] Joint017  label="Fixed003"  # Assembly joint (typed FeaturePython)
  Activated = true
  AngleMax = 0
  AngleMin = 0
  Detach1 = false
  Detach2 = false
  Distance = 0
  Distance2 = 0
  EnableAngleMax = false
  EnableAngleMin = false
  EnableLengthMax = false
  EnableLengthMin = false
  JointType = 0 (Fixed)
  LengthMax = 0
  LengthMin = 0
  Placement1 = pos=(358.5,75,11.5) rot=(0,0.707107,0.707107;3.14159rad)
  Placement2 = pos=(0,6.53e-14,283) rot=(1,0,0;1.5708rad)
  Reference1 = -> Assembly [Plank002.Edge11,Plank002.Edge11]
  Reference2 = -> Assembly [Strip001.Edge47,Strip001.Edge47]
FEATURE [App::FeaturePython] Joint018  label="Fixed004"  # Assembly joint (typed FeaturePython)
  Activated = true
  AngleMax = 0
  AngleMin = 0
  Detach1 = false
  Detach2 = false
  Distance = 0
  Distance2 = 0
  EnableAngleMax = false
  EnableAngleMin = false
  EnableLengthMax = false
  EnableLengthMin = false
  JointType = 0 (Fixed)
  LengthMax = 0
  LengthMin = 0
  Placement1 = pos=(-358.5,75,11.5) rot=(0,0.707107,0.707107;3.14159rad)
  Placement2 = pos=(1.1e-15,6.51e-14,283) rot=(1,0,0;1.5708rad)
  Reference1 = -> Assembly [Plank002.Edge12,Plank002.Edge12]
  Reference2 = -> Assembly [Strip.Edge47,Strip.Edge47]
FEATURE [App::FeaturePython] Joint019  label="Fixed005"  # Assembly joint (typed FeaturePython)
  Activated = true
  AngleMax = 0
  AngleMin = 0
  Detach1 = false
  Detach2 = false
  Distance = 0
  Distance2 = 0
  EnableAngleMax = false
  EnableAngleMin = false
  EnableLengthMax = false
  EnableLengthMin = false
  JointType = 0 (Fixed)
  LengthMax = 0
  LengthMin = 0
  Placement1 = pos=(56.25,-11.5,45) rot=(-0.707107,0,-0.707107;3.14159rad)
  Placement2 = pos=(-1.2e-15,-4.68e-14,-204.5) rot=(1,0,0;1.5708rad)
  Reference1 = -> Assembly [Triangle005.Edge12,Triangle005.Edge12]
  Reference2 = -> Assembly [Strip.Edge29,Strip.Edge29]
FEATURE [App::FeaturePython] Joint020  label="Parallel011"  # Assembly joint (typed FeaturePython)
  Activated = true
  AngleMax = 0
  AngleMin = 0
  Detach1 = false
  Detach2 = false
  Distance = 0
  Distance2 = 0
  EnableAngleMax = false
  EnableAngleMin = false
  EnableLengthMax = false
  EnableLengthMin = false
  JointType = 6 (Parallel)
  LengthMax = 0
  LengthMin = 0
  Placement1 = pos=(56.25,-1.24e-14,0) rot=(0,0,1;0rad)
  Placement2 = pos=(11.5,-7.57e-14,-324.5) rot=(0,0,1;1.5708rad)
  Reference1 = -> Assembly [Triangle005.Edge8,Triangle005.Edge8]
  Reference2 = -> Assembly [Strip.Edge9,Strip.Vertex5]
FEATURE [App::FeaturePython] Joint021  label="Fixed006"  # Assembly joint (typed FeaturePython)
  Activated = true
  AngleMax = 0
  AngleMin = 0
  Detach1 = false
  Detach2 = false
  Distance = 0
  Distance2 = 0
  EnableAngleMax = false
  EnableAngleMin = false
  EnableLengthMax = false
  EnableLengthMin = false
  JointType = 0 (Fixed)
  LengthMax = 0
  LengthMin = 0
  Placement1 = pos=(0,-7.5e-15,18.5) rot=(1,0,0;1.5708rad)
  Placement2 = pos=(56.25,-11.5,45) rot=(-0.707107,0,-0.707107;3.14159rad)
  Reference1 = -> Assembly [Strip001.Edge41,Strip001.Edge41]
  Reference2 = -> Assembly [Triangle003.Edge12,Triangle003.Edge12]
FEATURE [App::FeaturePython] Joint022  label="Parallel012"  # Assembly joint (typed FeaturePython)
  Activated = true
  AngleMax = 0
  AngleMin = 0
  Detach1 = false
  Detach2 = false
  Distance = 0
  Distance2 = 0
  EnableAngleMax = false
  EnableAngleMin = false
  EnableLengthMax = false
  EnableLengthMin = false
  JointType = 6 (Parallel)
  LengthMax = 0
  LengthMin = 0
  Placement1 = pos=(56.25,0,1.78e-14) rot=(0,0,1;0rad)
  Placement2 = pos=(11.5,-1.47e-14,-2.16e-14) rot=(0,0,1;1.5708rad)
  Reference1 = -> Assembly [Triangle003.Edge8,Triangle003.Edge8]
  Reference2 = -> Assembly [Strip001.Edge9,Strip001.Edge9]
FEATURE [App::FeaturePython] Joint023  label="Fixed007"  # Assembly joint (typed FeaturePython)
  Activated = true
  AngleMax = 0
  AngleMin = 0
  Detach1 = false
  Detach2 = false
  Distance = 0
  Distance2 = 0
  EnableAngleMax = false
  EnableAngleMin = false
  EnableLengthMax = false
  EnableLengthMin = false
  JointType = 0 (Fixed)
  LengthMax = 0
  LengthMin = 0
  Placement1 = pos=(56.25,-11.5,45) rot=(-0.707107,0,-0.707107;3.14159rad)
  Placement2 = pos=(1.137e-13,-2.84e-14,-204.5) rot=(1,0,0;1.5708rad)
  Reference1 = -> Assembly [Triangle004.Edge12,Triangle004.Edge12]
  Reference2 = -> Assembly [Strip001.Edge29,Strip001.Edge29]
FEATURE [App::FeaturePython] Joint024  label="Parallel013"  # Assembly joint (typed FeaturePython)
  Activated = true
  AngleMax = 0
  AngleMin = 0
  Detach1 = false
  Detach2 = false
  Distance = 0
  Distance2 = 0
  EnableAngleMax = false
  EnableAngleMin = false
  EnableLengthMax = false
  EnableLengthMin = false
  JointType = 6 (Parallel)
  LengthMax = 0
  LengthMin = 0
  Placement1 = pos=(56.25,-23,0) rot=(0,0,1;0rad)
  Placement2 = pos=(-11.5,-7.2e-14,-324.5) rot=(-0.707107,0.707107,0;3.14159rad)
  Reference1 = -> Assembly [Triangle004.Edge9,Triangle004.Edge9]
  Reference2 = -> Assembly [Strip001.Edge3,Strip001.Vertex3]
FEATURE [App::FeaturePython] Joint025  label="Fixed008"  # Assembly joint (typed FeaturePython)
  Activated = true
  AngleMax = 0
  AngleMin = 0
  Detach1 = false
  Detach2 = false
  Distance = 0
  Distance2 = 0
  EnableAngleMax = false
  EnableAngleMin = false
  EnableLengthMax = false
  EnableLengthMin = false
  JointType = 0 (Fixed)
  LengthMax = 0
  LengthMin = 0
  Placement1 = pos=(358.5,75,11.5) rot=(0,-0.707107,-0.707107;3.14159rad)
  Placement2 = pos=(0,1.35e-14,60) rot=(1,0,0;1.5708rad)
  Reference1 = -> Assembly [Plank.Edge11,Plank.Edge11]
  Reference2 = -> Assembly [Strip.Edge38,Strip.Edge38]
FEATURE [App::FeaturePython] Joint026  label="Parallel014"  # Assembly joint (typed FeaturePython)
  Activated = true
  AngleMax = 0
  AngleMin = 0
  Detach1 = false
  Detach2 = false
  Distance = 0
  Distance2 = 0
  EnableAngleMax = false
  EnableAngleMin = false
  EnableLengthMax = false
  EnableLengthMin = false
  JointType = 6 (Parallel)
  LengthMax = 0
  LengthMin = 0
  Placement1 = pos=(-400,0,0) rot=(-0.57735,-0.57735,0.57735;4.18879rad)
  Placement2 = pos=(-1.42e-14,1.137e-13,75) rot=(-0.707107,0,0.707107;3.14159rad)
  Reference1 = -> Assembly [Plank.Edge13,Plank.Edge13]
  Reference2 = -> Assembly [Triangle003.Edge13,Triangle003.Edge13]
FEATURE [App::FeaturePython] Joint027  label="Fixed009"  # Assembly joint (typed FeaturePython)
  Activated = true
  AngleMax = 0
  AngleMin = 0
  Detach1 = false
  Detach2 = false
  Distance = 0
  Distance2 = 0
  EnableAngleMax = false
  EnableAngleMin = false
  EnableLengthMax = false
  EnableLengthMin = false
  JointType = 0 (Fixed)
  LengthMax = 0
  LengthMin = 0
  Placement1 = pos=(358.5,75,11.5) rot=(0,-0.707107,-0.707107;3.14159rad)
  Placement2 = pos=(4.1e-15,-3.67e-14,-163) rot=(1,0,0;1.5708rad)
  Reference1 = -> Assembly [Plank001.Edge11,Plank001.Edge11]
  Reference2 = -> Assembly [Strip.Edge26,Strip.Edge26]
FEATURE [App::FeaturePython] Joint028  label="Parallel015"  # Assembly joint (typed FeaturePython)
  Activated = true
  AngleMax = 0
  AngleMin = 0
  Detach1 = false
  Detach2 = false
  Distance = 0
  Distance2 = 0
  EnableAngleMax = false
  EnableAngleMin = false
  EnableLengthMax = false
  EnableLengthMin = false
  JointType = 6 (Parallel)
  LengthMax = 0
  LengthMin = 0
  Placement1 = pos=(400,0,-2.84e-14) rot=(0.57735,0.57735,0.57735;4.18879rad)
  Placement2 = pos=(-7.1e-15,-23,75) rot=(-0.707107,0,0.707107;3.14159rad)
  Reference1 = -> Assembly [Plank001.Edge3,Plank001.Edge3]
  Reference2 = -> Assembly [Triangle005.Edge15,Triangle005.Edge15]
FEATURE [TechDraw::DrawSVGTemplate] Template
  Height = 210
  Orientation = 1
  Template = /Applications/FreeCAD.app/Contents/Resources/share/Mod/TechDraw/Templates/Default_Template_A4_Landscape.svg
  Width = 297
FEATURE [TechDraw::DrawProjGroupItem] View  label="Triangle side"
  CoarseView = false
  Direction = (0,-1,0)
  Focus = 100
  HardHidden = false
  IsoCount = 0
  IsoHidden = false
  IsoVisible = false
  LockPosition = false
  Perspective = false
  Rotation = 0
  RotationVector = (1,0,0)
  ScaleType = 0
  ScrubCount = 1
  SeamHidden = false
  SeamVisible = false
  SmoothHidden = false
  SmoothVisible = true
  Source = -> [Body001]
  Type = 0
  X = 133.883
  XDirection = (1,0,0)
  Y = 99.4338
FEATURE [TechDraw::DrawViewDimension] Dimension
  AngleOverride = false
  Arbitrary = false
  ArbitraryTolerances = false
  BoxCorners = (2) [(-56.25,-75,0),(56.25,75,0)]
  EqualTolerance = true
  ExtensionAngle = 0
  FormatSpec = %.2w
  FormatSpecOverTolerance = %+.2w
  FormatSpecUnderTolerance = %+.2w
  Inverted = false
  LineAngle = 0
  LockPosition = false
  MeasureType = 1
  OverTolerance = 0
  References2D = -> [View]
  Rotation = 0
  ScaleType = 0
  TheoreticalExact = false
  Type = 0
  UnderTolerance = 0
  X = -68.1867
  Y = 50.4225
FEATURE [TechDraw::DrawViewDimension] Dimension001
  AngleOverride = false
  Arbitrary = false
  ArbitraryTolerances = false
  BoxCorners = (2) [(-56.25,-75,0),(56.25,75,0)]
  EqualTolerance = true
  ExtensionAngle = 0
  FormatSpec = %.2w
  FormatSpecOverTolerance = %+.2w
  FormatSpecUnderTolerance = %+.2w
  Inverted = false
  LineAngle = 0
  LockPosition = false
  MeasureType = 1
  OverTolerance = 0
  References2D = -> [View]
  Rotation = 0
  ScaleType = 0
  TheoreticalExact = false
  Type = 0
  UnderTolerance = 0
  X = 43.3402
  Y = -80.0994
FEATURE [TechDraw::DrawViewDimension] Dimension002
  AngleOverride = false
  Arbitrary = false
  ArbitraryTolerances = false
  BoxCorners = (2) [(-56.25,-75,0),(56.25,75,0)]
  EqualTolerance = true
  ExtensionAngle = 0
  FormatSpec = R%.2w
  FormatSpecOverTolerance = %+.2w
  FormatSpecUnderTolerance = %+.2w
  Inverted = false
  LineAngle = 0
  LockPosition = false
  MeasureType = 1
  OverTolerance = 0
  References2D = -> [View]
  Rotation = 0
  ScaleType = 0
  TheoreticalExact = false
  Type = 4
  UnderTolerance = 0
  X = -16.3877
  Y = -11.2275
FEATURE [TechDraw::DrawViewDimension] Dimension003
  AngleOverride = false
  Arbitrary = false
  ArbitraryTolerances = false
  BoxCorners = (2) [(-56.25,-75,0),(56.25,75,0)]
  EqualTolerance = true
  ExtensionAngle = 0
  FormatSpec = %.2w
  FormatSpecOverTolerance = %+.2w
  FormatSpecUnderTolerance = %+.2w
  Inverted = false
  LineAngle = 0
  LockPosition = false
  MeasureType = 1
  OverTolerance = 0
  References2D = -> [View]
  Rotation = 0
  ScaleType = 0
  TheoreticalExact = false
  Type = 2
  UnderTolerance = 0
  X = 69.6221
  Y = 0
FEATURE [TechDraw::DrawViewDimension] Dimension004
  AngleOverride = false
  Arbitrary = false
  ArbitraryTolerances = false
  BoxCorners = (2) [(-56.25,-75,0),(56.25,75,0)]
  EqualTolerance = true
  ExtensionAngle = 0
  FormatSpec = %.2w
  FormatSpecOverTolerance = %+.2w
  FormatSpecUnderTolerance = %+.2w
  Inverted = false
  LineAngle = 0
  LockPosition = false
  MeasureType = 1
  OverTolerance = 0
  References2D = -> [View]
  Rotation = 0
  ScaleType = 0
  TheoreticalExact = false
  Type = 1
  UnderTolerance = 0
  X = 0
  Y = 87.4372
FEATURE [TechDraw::DrawPage] Page  label="Triangle Page"
  KeepUpdated = true
  NextBalloonIndex = 1
  ProjectionType = 0
  Template = -> Template
  Views = -> [View,Dimension,Dimension001,Dimension002,Dimension003,Dimension004]
FEATURE [TechDraw::DrawSVGTemplate] Template001
  Height = 210
  Orientation = 1
  Template = /Applications/FreeCAD.app/Contents/Resources/share/Mod/TechDraw/Templates/Default_Template_A4_Landscape.svg
  Width = 297
FEATURE [TechDraw::DrawProjGroupItem] View001  label="Strip top"
  CoarseView = false
  Direction = (0,-1,0)
  Focus = 100
  HardHidden = false
  IsoCount = 0
  IsoHidden = false
  IsoVisible = false
  LockPosition = false
  Perspective = false
  Rotation = 0
  RotationVector = (1,0,0)
  Scale = 0.428571
  ScaleType = 2
  ScrubCount = 1
  SeamHidden = false
  SeamVisible = false
  SmoothHidden = false
  SmoothVisible = true
  Source = -> [Body002]
  Type = 0
  X = 151.9
  XDirection = (1e-16,0,-1)
  Y = 112.651
FEATURE [TechDraw::DrawViewDimension] Dimension005
  AngleOverride = false
  Arbitrary = false
  ArbitraryTolerances = false
  BoxCorners = (2) [(-141.536,-4.92857,0),(141.536,4.92857,0)]
  EqualTolerance = true
  ExtensionAngle = 0
  FormatSpec = ⌀%.2w
  FormatSpecOverTolerance = %+.2w
  FormatSpecUnderTolerance = %+.2w
  Inverted = false
  LineAngle = 0
  LockPosition = false
  MeasureType = 1
  OverTolerance = 0
  References2D = -> [View001]
  Rotation = 0
  ScaleType = 0
  TheoreticalExact = false
  Type = 5
  UnderTolerance = 0
  X = -49.6802
  Y = 1.28275
FEATURE [TechDraw::DrawViewDimension] Dimension006
  AngleOverride = false
  Arbitrary = false
  ArbitraryTolerances = false
  BoxCorners = (2) [(-141.536,-4.92857,0),(141.536,4.92857,0)]
  EqualTolerance = true
  ExtensionAngle = 0
  FormatSpec = R%.2w
  FormatSpecOverTolerance = %+.2w
  FormatSpecUnderTolerance = %+.2w
  Inverted = false
  LineAngle = 0
  LockPosition = false
  MeasureType = 1
  OverTolerance = 0
  References2D = -> [View001]
  Rotation = 0
  ScaleType = 0
  TheoreticalExact = false
  Type = 4
  UnderTolerance = 0
  X = -143.796
  Y = 39.867
FEATURE [TechDraw::DrawViewDimension] Dimension008
  AngleOverride = false
  Arbitrary = false
  ArbitraryTolerances = false
  BoxCorners = (2) [(-141.536,-4.92857,0),(141.536,4.92857,0)]
  EqualTolerance = true
  ExtensionAngle = 0
  FormatSpec = %.2w
  FormatSpecOverTolerance = %+.2w
  FormatSpecUnderTolerance = %+.2w
  Inverted = false
  LineAngle = 0
  LockPosition = false
  MeasureType = 1
  OverTolerance = 0
  References2D = -> [View001]
  Rotation = 0
  ScaleType = 0
  TheoreticalExact = false
  Type = 0
  UnderTolerance = 0
  X = 106.907
  Y = 0
FEATURE [TechDraw::DrawViewDimension] Dimension009
  AngleOverride = false
  Arbitrary = false
  ArbitraryTolerances = false
  BoxCorners = (2) [(-141.536,-4.92857,0),(141.536,4.92857,0)]
  EqualTolerance = true
  ExtensionAngle = 0
  FormatSpec = %.2w
  FormatSpecOverTolerance = %+.2w
  FormatSpecUnderTolerance = %+.2w
  Inverted = false
  LineAngle = 0
  LockPosition = false
  MeasureType = 1
  OverTolerance = 0
  References2D = -> [View001]
  Rotation = 0
  ScaleType = 0
  TheoreticalExact = false
  Type = 1
  UnderTolerance = 0
  X = 2.46429
  Y = -36.7016
FEATURE [TechDraw::DrawViewDimension] Dimension010
  AngleOverride = false
  Arbitrary = false
  ArbitraryTolerances = false
  BoxCorners = (2) [(-141.536,-4.92857,0),(141.536,4.92857,0)]
  EqualTolerance = true
  ExtensionAngle = 0
  FormatSpec = %.2w
  FormatSpecOverTolerance = %+.2w
  FormatSpecUnderTolerance = %+.2w
  Inverted = false
  LineAngle = 0
  LockPosition = false
  MeasureType = 1
  OverTolerance = 0
  References2D = -> [View001]
  Rotation = 0
  ScaleType = 0
  TheoreticalExact = false
  Type = 1
  UnderTolerance = 0
  X = 135.107
  Y = -9.26061
FEATURE [TechDraw::DrawViewDimension] Dimension011
  AngleOverride = false
  Arbitrary = false
  ArbitraryTolerances = false
  BoxCorners = (2) [(-141.536,-4.92857,0),(141.536,4.92857,0)]
  EqualTolerance = true
  ExtensionAngle = 0
  FormatSpec = %.2w
  FormatSpecOverTolerance = %+.2w
  FormatSpecUnderTolerance = %+.2w
  Inverted = false
  LineAngle = 0
  LockPosition = false
  MeasureType = 1
  OverTolerance = 0
  References2D = -> [View001]
  Rotation = 0
  ScaleType = 0
  TheoreticalExact = false
  Type = 1
  UnderTolerance = 0
  X = 105.302
  Y = -13.2083
FEATURE [TechDraw::DrawViewDimension] Dimension012
  AngleOverride = false
  Arbitrary = false
  ArbitraryTolerances = false
  BoxCorners = (2) [(-141.536,-4.92857,0),(141.536,4.92857,0)]
  EqualTolerance = true
  ExtensionAngle = 0
  FormatSpec = %.2w
  FormatSpecOverTolerance = %+.2w
  FormatSpecUnderTolerance = %+.2w
  Inverted = false
  LineAngle = 0
  LockPosition = false
  MeasureType = 1
  OverTolerance = 0
  References2D = -> [View001]
  Rotation = 0
  ScaleType = 0
  TheoreticalExact = false
  Type = 1
  UnderTolerance = 0
  X = 106.929
  Y = -22.368
FEATURE [TechDraw::DrawViewDimension] Dimension013
  AngleOverride = false
  Arbitrary = false
  ArbitraryTolerances = false
  BoxCorners = (2) [(-141.536,-4.92857,0),(141.536,4.92857,0)]
  EqualTolerance = true
  ExtensionAngle = 0
  FormatSpec = %.2w
  FormatSpecOverTolerance = %+.2w
  FormatSpecUnderTolerance = %+.2w
  Inverted = false
  LineAngle = 0
  LockPosition = false
  MeasureType = 1
  OverTolerance = 0
  References2D = -> [View001]
  Rotation = 0
  ScaleType = 0
  TheoreticalExact = false
  Type = 1
  UnderTolerance = 0
  X = 61.0191
  Y = -29.368
FEATURE [TechDraw::DrawViewDimension] Dimension014
  AngleOverride = false
  Arbitrary = false
  ArbitraryTolerances = false
  BoxCorners = (2) [(-141.536,-4.92857,0),(141.536,4.92857,0)]
  EqualTolerance = true
  ExtensionAngle = 0
  FormatSpec = %.2w
  FormatSpecOverTolerance = %+.2w
  FormatSpecUnderTolerance = %+.2w
  Inverted = false
  LineAngle = 0
  LockPosition = false
  MeasureType = 1
  OverTolerance = 0
  References2D = -> [View001]
  Rotation = 0
  ScaleType = 0
  TheoreticalExact = false
  Type = 1
  UnderTolerance = 0
  X = 68.0357
  Y = 14.3692
FEATURE [TechDraw::DrawViewDimension] Dimension015
  AngleOverride = false
  Arbitrary = false
  ArbitraryTolerances = false
  BoxCorners = (2) [(-141.536,-4.92857,0),(141.536,4.92857,0)]
  EqualTolerance = true
  ExtensionAngle = 0
  FormatSpec = %.2w
  FormatSpecOverTolerance = %+.2w
  FormatSpecUnderTolerance = %+.2w
  Inverted = false
  LineAngle = 0
  LockPosition = false
  MeasureType = 1
  OverTolerance = 0
  References2D = -> [View001]
  Rotation = 0
  ScaleType = 0
  TheoreticalExact = false
  Type = 1
  UnderTolerance = 0
  X = 53.7947
  Y = 23.2621
FEATURE [TechDraw::DrawViewDimension] Dimension016
  AngleOverride = false
  Arbitrary = false
  ArbitraryTolerances = false
  BoxCorners = (2) [(-141.536,-4.92857,0),(141.536,4.92857,0)]
  EqualTolerance = true
  ExtensionAngle = 0
  FormatSpec = %.2w
  FormatSpecOverTolerance = %+.2w
  FormatSpecUnderTolerance = %+.2w
  Inverted = false
  LineAngle = 0
  LockPosition = false
  MeasureType = 1
  OverTolerance = 0
  References2D = -> [View001]
  Rotation = 0
  ScaleType = 0
  TheoreticalExact = false
  Type = 1
  UnderTolerance = 0
  X = 24.1898
  Y = 34.3147
FEATURE [TechDraw::DrawViewDimension] Dimension017
  AngleOverride = false
  Arbitrary = false
  ArbitraryTolerances = false
  BoxCorners = (2) [(-141.536,-4.92857,0),(141.536,4.92857,0)]
  EqualTolerance = true
  ExtensionAngle = 0
  FormatSpec = %.2w
  FormatSpecOverTolerance = %+.2w
  FormatSpecUnderTolerance = %+.2w
  Inverted = false
  LineAngle = 0
  LockPosition = false
  MeasureType = 1
  OverTolerance = 0
  References2D = -> [View001]
  Rotation = 0
  ScaleType = 0
  TheoreticalExact = false
  Type = 1
  UnderTolerance = 0
  X = 3.35647
  Y = 45.2309
FEATURE [TechDraw::DrawViewDimension] Dimension018
  AngleOverride = false
  Arbitrary = false
  ArbitraryTolerances = false
  BoxCorners = (2) [(-141.536,-4.92857,0),(141.536,4.92857,0)]
  EqualTolerance = true
  ExtensionAngle = 0
  FormatSpec = %.2w
  FormatSpecOverTolerance = %+.2w
  FormatSpecUnderTolerance = %+.2w
  Inverted = false
  LineAngle = 0
  LockPosition = false
  MeasureType = 1
  OverTolerance = 0
  References2D = -> [View001]
  Rotation = 0
  ScaleType = 0
  TheoreticalExact = false
  Type = 1
  UnderTolerance = 0
  X = 11.3571
  Y = 60.8571
FEATURE [TechDraw::DrawSVGTemplate] Template002
  Height = 210
  Orientation = 1
  Template = /Applications/FreeCAD.app/Contents/Resources/share/Mod/TechDraw/Templates/Default_Template_A4_Landscape.svg
  Width = 297
FEATURE [TechDraw::DrawProjGroupItem] View002  label="Front"
  CoarseView = false
  Direction = (0,-1,0)
  Focus = 100
  HardHidden = false
  IsoCount = 0
  IsoHidden = false
  IsoVisible = false
  LockPosition = true
  Perspective = false
  Rotation = 0
  RotationVector = (1,0,0)
  Scale = 0.333333
  ScaleType = 2
  ScrubCount = 1
  SeamHidden = false
  SeamVisible = false
  SmoothHidden = false
  SmoothVisible = true
  Source = -> [Body]
  Type = 0
  X = 0
  XDirection = (1,0,0)
  Y = 0
FEATURE [TechDraw::DrawProjGroupItem] ProjItem002  label="Top"
  CoarseView = false
  Direction = (0,0,1)
  Focus = 100
  HardHidden = false
  IsoCount = 0
  IsoHidden = false
  IsoVisible = false
  LockPosition = false
  Perspective = false
  Rotation = 0
  RotationVector = (1,0,0)
  Scale = 0.333333
  ScaleType = 2
  ScrubCount = 1
  SeamHidden = false
  SeamVisible = false
  SmoothHidden = false
  SmoothVisible = true
  Source = -> [Body]
  Type = 4
  X = 0
  XDirection = (1,0,0)
  Y = -97.3091
FEATURE [TechDraw::DrawProjGroup] ProjGroup
  Anchor = -> View002
  AutoDistribute = true
  LockPosition = false
  ProjectionType = 0
  Rotation = 0
  Scale = 0.333333
  ScaleType = 2
  Source = -> [Body]
  Views = -> [View002,ProjItem002]
  X = 153.411
  Y = 179.866
  spacingX = 15
  spacingY = 15
FEATURE [TechDraw::DrawViewDimension] Dimension019
  AngleOverride = false
  Arbitrary = false
  ArbitraryTolerances = false
  BoxCorners = (2) [(-133.333,-25,0),(133.333,25,0)]
  EqualTolerance = true
  ExtensionAngle = 0
  FormatSpec = %.2w
  FormatSpecOverTolerance = %+.2w
  FormatSpecUnderTolerance = %+.2w
  Inverted = false
  LineAngle = 0
  LockPosition = false
  MeasureType = 1
  OverTolerance = 0
  References2D = -> [ProjItem002]
  Rotation = 0
  ScaleType = 0
  TheoreticalExact = false
  Type = 1
  UnderTolerance = 0
  X = 0
  Y = 8.51604
FEATURE [TechDraw::DrawViewDimension] Dimension020
  AngleOverride = false
  Arbitrary = false
  ArbitraryTolerances = false
  BoxCorners = (2) [(-133.333,-25,0),(133.333,25,0)]
  EqualTolerance = true
  ExtensionAngle = 0
  FormatSpec = %.2w
  FormatSpecOverTolerance = %+.2w
  FormatSpecUnderTolerance = %+.2w
  Inverted = false
  LineAngle = 0
  LockPosition = false
  MeasureType = 1
  OverTolerance = 0
  References2D = -> [ProjItem002]
  Rotation = 0
  ScaleType = 0
  TheoreticalExact = false
  Type = 2
  UnderTolerance = 0
  X = -143.573
  Y = 0
FEATURE [TechDraw::DrawViewDimension] Dimension021
  AngleOverride = false
  Arbitrary = false
  ArbitraryTolerances = false
  BoxCorners = (2) [(-133.333,-3.83333,0),(133.333,3.83333,0)]
  EqualTolerance = true
  ExtensionAngle = 0
  FormatSpec = %.2w
  FormatSpecOverTolerance = %+.2w
  FormatSpecUnderTolerance = %+.2w
  Inverted = false
  LineAngle = 0
  LockPosition = false
  MeasureType = 1
  OverTolerance = 0
  References2D = -> [View002]
  Rotation = 0
  ScaleType = 0
  TheoreticalExact = false
  Type = 2
  UnderTolerance = 0
  X = -143.227
  Y = -8.60517
FEATURE [TechDraw::DrawViewDimension] Dimension022
  AngleOverride = false
  Arbitrary = false
  ArbitraryTolerances = false
  BoxCorners = (2) [(-133.333,-25,0),(133.333,25,0)]
  EqualTolerance = true
  ExtensionAngle = 0
  FormatSpec = %.2w
  FormatSpecOverTolerance = %+.2w
  FormatSpecUnderTolerance = %+.2w
  Inverted = false
  LineAngle = 0
  LockPosition = false
  MeasureType = 1
  OverTolerance = 0
  References2D = -> [ProjItem002]
  Rotation = 0
  ScaleType = 0
  TheoreticalExact = false
  Type = 2
  UnderTolerance = 0
  X = -81.4492
  Y = 52.8497
FEATURE [TechDraw::DrawViewDimension] Dimension023
  AngleOverride = false
  Arbitrary = false
  ArbitraryTolerances = false
  BoxCorners = (2) [(-133.333,-25,0),(133.333,25,0)]
  EqualTolerance = true
  ExtensionAngle = 0
  FormatSpec = %.2w
  FormatSpecOverTolerance = %+.2w
  FormatSpecUnderTolerance = %+.2w
  Inverted = false
  LineAngle = 0
  LockPosition = false
  MeasureType = 1
  OverTolerance = 0
  References2D = -> [ProjItem002]
  Rotation = 0
  ScaleType = 0
  TheoreticalExact = false
  Type = 2
  UnderTolerance = 0
  X = -115.26
  Y = -15
FEATURE [TechDraw::DrawViewDimension] Dimension024
  AngleOverride = false
  Arbitrary = false
  ArbitraryTolerances = false
  BoxCorners = (2) [(-133.333,-25,0),(133.333,25,0)]
  EqualTolerance = true
  ExtensionAngle = 0
  FormatSpec = %.2w
  FormatSpecOverTolerance = %+.2w
  FormatSpecUnderTolerance = %+.2w
  Inverted = false
  LineAngle = 0
  LockPosition = false
  MeasureType = 1
  OverTolerance = 0
  References2D = -> [ProjItem002]
  Rotation = 0
  ScaleType = 0
  TheoreticalExact = false
  Type = 1
  UnderTolerance = 0
  X = 96.1182
  Y = 42.3752
FEATURE [TechDraw::DrawViewDimension] Dimension025
  AngleOverride = false
  Arbitrary = false
  ArbitraryTolerances = false
  BoxCorners = (2) [(-133.333,-3.83333,0),(133.333,3.83333,0)]
  EqualTolerance = true
  ExtensionAngle = 0
  FormatSpec = %.2w
  FormatSpecOverTolerance = %+.2w
  FormatSpecUnderTolerance = %+.2w
  Inverted = false
  LineAngle = 0
  LockPosition = false
  MeasureType = 1
  OverTolerance = 0
  References2D = -> [View002]
  Rotation = 0
  ScaleType = 0
  TheoreticalExact = false
  Type = 1
  UnderTolerance = 0
  X = -13.3457
  Y = 20.202
FEATURE [TechDraw::DrawViewDimension] Dimension026
  AngleOverride = false
  Arbitrary = false
  ArbitraryTolerances = false
  BoxCorners = (2) [(-133.333,-25,0),(133.333,25,0)]
  EqualTolerance = true
  ExtensionAngle = 0
  FormatSpec = ⌀%.2w
  FormatSpecOverTolerance = %+.2w
  FormatSpecUnderTolerance = %+.2w
  Inverted = false
  LineAngle = 0
  LockPosition = false
  MeasureType = 1
  OverTolerance = 0
  References2D = -> [ProjItem002]
  Rotation = 0
  ScaleType = 0
  TheoreticalExact = false
  Type = 5
  UnderTolerance = 0
  X = 125.039
  Y = -15.9913
FEATURE [TechDraw::DrawPage] Page002  label="Plank Page"
  KeepUpdated = true
  NextBalloonIndex = 1
  ProjectionType = 0
  Template = -> Template002
  Views = -> [ProjGroup,Dimension019,Dimension020,Dimension021,Dimension022,Dimension023,Dimension024,Dimension025,Dimension026]
FEATURE [TechDraw::DrawViewDimension] Dimension027
  AngleOverride = false
  Arbitrary = false
  ArbitraryTolerances = false
  BoxCorners = (2) [(-141.536,-4.92857,0),(141.536,4.92857,0)]
  EqualTolerance = true
  ExtensionAngle = 0
  FormatSpec = R%.2w
  FormatSpecOverTolerance = %+.2w
  FormatSpecUnderTolerance = %+.2w
  Inverted = false
  LineAngle = 0
  LockPosition = false
  MeasureType = 1
  OverTolerance = 0
  References2D = -> [View001]
  Rotation = 0
  ScaleType = 0
  TheoreticalExact = false
  Type = 4
  UnderTolerance = 0
  X = -105.575
  Y = 42.057
FEATURE [TechDraw::DrawViewDimension] Dimension028
  AngleOverride = false
  Arbitrary = false
  ArbitraryTolerances = false
  BoxCorners = (2) [(-141.536,-4.92857,0),(141.536,4.92857,0)]
  EqualTolerance = true
  ExtensionAngle = 0
  FormatSpec = %.2w
  FormatSpecOverTolerance = %+.2w
  FormatSpecUnderTolerance = %+.2w
  Inverted = false
  LineAngle = 0
  LockPosition = false
  MeasureType = 1
  OverTolerance = 0
  References2D = -> [View001]
  Rotation = 0
  ScaleType = 0
  TheoreticalExact = false
  Type = 1
  UnderTolerance = 0
  X = -87.4546
  Y = -26.4549
FEATURE [TechDraw::DrawViewDimension] Dimension029
  AngleOverride = false
  Arbitrary = false
  ArbitraryTolerances = false
  BoxCorners = (2) [(-141.536,-4.92857,0),(141.536,4.92857,0)]
  EqualTolerance = true
  ExtensionAngle = 0
  FormatSpec = %.2w
  FormatSpecOverTolerance = %+.2w
  FormatSpecUnderTolerance = %+.2w
  Inverted = false
  LineAngle = 0
  LockPosition = false
  MeasureType = 1
  OverTolerance = 0
  References2D = -> [View001]
  Rotation = 0
  ScaleType = 0
  TheoreticalExact = false
  Type = 1
  UnderTolerance = 0
  X = -134.464
  Y = 23.2621
FEATURE [TechDraw::DrawViewDimension] Dimension030
  AngleOverride = false
  Arbitrary = false
  ArbitraryTolerances = false
  BoxCorners = (2) [(-141.536,-4.92857,0),(141.536,4.92857,0)]
  EqualTolerance = true
  ExtensionAngle = 0
  FormatSpec = %.2w
  FormatSpecOverTolerance = %+.2w
  FormatSpecUnderTolerance = %+.2w
  Inverted = false
  LineAngle = 0
  LockPosition = false
  MeasureType = 1
  OverTolerance = 0
  References2D = -> [View001]
  Rotation = 0
  ScaleType = 0
  TheoreticalExact = false
  Type = 0
  UnderTolerance = 0
  X = -148.369
  Y = -51.4303
FEATURE [TechDraw::DrawPage] Page001  label="Strip page"
  KeepUpdated = true
  NextBalloonIndex = 1
  ProjectionType = 0
  Template = -> Template001
  Views = -> [View001,Dimension005,Dimension006,Dimension008,Dimension009,Dimension010,Dimension011,Dimension012,Dimension013,Dimension014,Dimension015,Dimension016,Dimension017,Dimension018,Dimension027,Dimension028,Dimension029,Dimension030]
FEATURE [App::FeaturePython] Joint029  label="Fixed010"  # Assembly joint (typed FeaturePython)
  Activated = true
  AngleMax = 0
  AngleMin = 0
  Detach1 = false
  Detach2 = false
  Distance = 0
  Distance2 = 0
  EnableAngleMax = false
  EnableAngleMin = false
  EnableLengthMax = false
  EnableLengthMin = false
  JointType = 0 (Fixed)
  LengthMax = 0
  LengthMin = 0
  Placement1 = pos=(-33.75,-11.5,75) rot=(0,0,-1;3.14159rad)
  Placement2 = pos=(358.5,-15,0) rot=(0,0,1;0rad)
  Reference1 = -> Assembly [Triangle002.Edge19,Triangle002.Edge19]
  Reference2 = -> Assembly [Plank002.Sketch005.Edge3,Plank002.Sketch005.Edge3]
FEATURE [Assembly::JointGroup] Joints
  Group = -> [GroundedJoint,Joint,Joint001,Joint002,Joint003,Joint004,Joint005,Joint006,Joint008,Joint009,Joint010,Joint011,Joint012,Joint013,Joint014,Joint015,Joint016,Joint017,Joint018,Joint019,Joint020,Joint021,Joint022,Joint023,Joint024,Joint025,Joint026,Joint027,Joint028,Joint029]
FEATURE [Assembly::AssemblyObject] Assembly
  Group = -> [Joints,Strip,Strip001,Triangle,Triangle001,Triangle002,Triangle003,Triangle004,Triangle005,Plank,Plank001,Plank002,GroundedJoint,Joint,Joint001,Joint002,Joint003,Joint004,Joint005,Joint006,Joint008,Joint009,Joint010,Joint011,Joint012,Joint013,Joint014,Joint015,Joint016,Joint017,Joint018,Joint019,Joint020,Joint021,Joint022,Joint023,Joint024,Joint025,Joint026,Joint027,Joint028,Joint029]
  Origin = -> Origin003
  Type = Assembly
